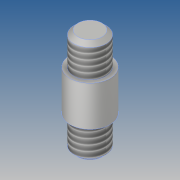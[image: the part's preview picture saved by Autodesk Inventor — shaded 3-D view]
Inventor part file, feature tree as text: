
AUTODESK INVENTOR PART (.ipt)
format: ipt  version: 2019 (Build 230136000, 136)  size: 105,984 bytes
history: native  units: mm
features: extrude x2, sketch x2, other x1, chamfer x1, mirror x1
ambient origin geometry x8: Origin, YZ Plane, XZ Plane, XY Plane, X Axis, Y Axis, Z Axis, Center Point
bodies: Solide1 (feature_tree)
feature tree (7):
  extrude  "Extrusion1"  Depth=5.0mm
  extrude  "Extrusion2"  Depth=5.0mm TaperAngle=0.0deg
  other  "Filetage1"
  chamfer  "Chanfrein1"  Distance=4.0mm
  mirror  "Symétrie1"
  sketch  "Esquisse1"
  sketch  "Esquisse2"
